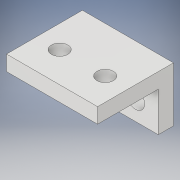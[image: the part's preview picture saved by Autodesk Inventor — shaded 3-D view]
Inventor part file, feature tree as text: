
AUTODESK INVENTOR PART (.ipt)
format: ipt  version: 2017 (Build 210142000, 142)  size: 127,488 bytes
history: native  units: in
note: dims shown in document units (in); Inventor stores cm internally (conversion verified against a paired STEP export)
features: sketch x3, hole x2, projected_geometry x2, extrude x1
ambient origin geometry x8: Origin, YZ Plane, XZ Plane, XY Plane, X Axis, Y Axis, Z Axis, Center Point
bodies: Solid1 (feature_tree)
feature tree (8):
  extrude  "Extrusion1"  Depth=0.625in
  hole  "Hole1"  [1 undecoded]
  hole  "Hole2"  [1 undecoded]
  sketch  "Sketch1"  dims[d0=0.45in d1=0.625in]
  sketch  "Sketch2"  dims[d2=0.325in d3=0.5in]
  projected_geometry  "Projected Loop1"
  sketch  "Sketch3"  dims[d4=0.75in d5=0.0in d6=0.375in d7=0.1875in d8=0.625in d11=0.135in d12=0.75in d13=0.375in d14=0.25in d15=0.5635in d16=1.0in d17=0.8108in d18=0.375in d19=0.375in d20=0.375in d21=0.1875in d22=0.1625in d23=0.1625in d24=0.15in d25=0.75in d26=0.375in d27=0.25in d28=0.5635in d29=1.0in d30=0.8108in d31=0.75in d32=0.75in d33=0.325in]
  projected_geometry  "Projected Loop2"
note: 2 required parameter values undecoded (feature->parameter linkage not recoverable at this tier; creation-order binding heuristic only, values carry confidence <= 0.55)
